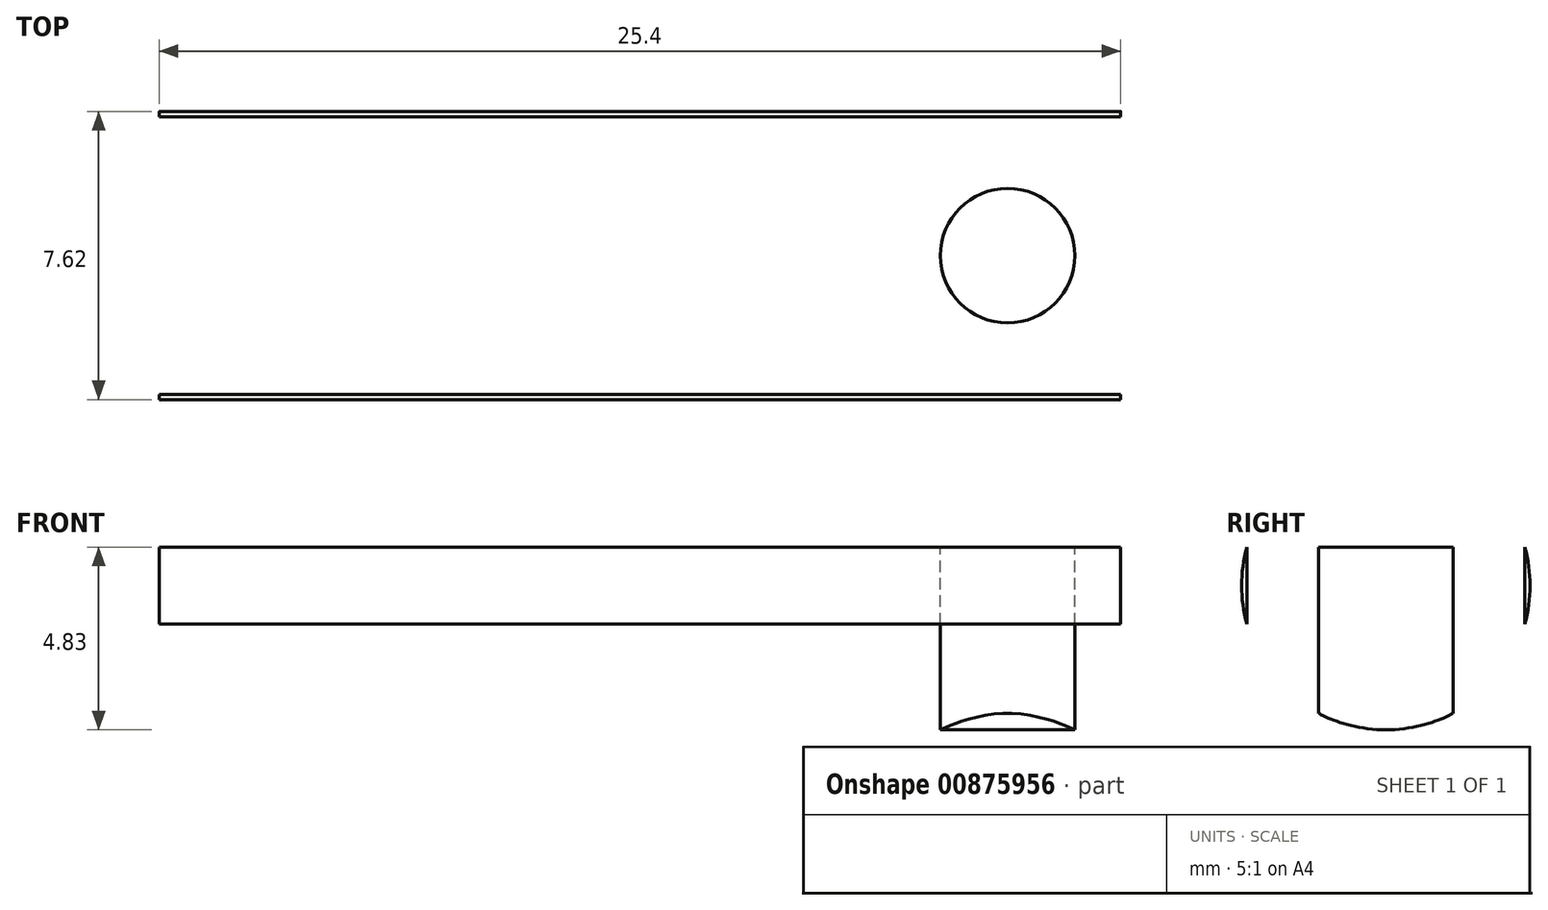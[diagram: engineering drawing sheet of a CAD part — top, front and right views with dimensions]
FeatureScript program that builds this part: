
annotation { "Feature Type Name" : "Feature", "Feature Type Description" : "" }
export const myFeature = defineFeature(function(context is Context, id is Id, definition is map)
    precondition{}
    {
        {
            var Q0;
            Q0=qCreatedBy(makeId("Right.planeOp"),FACE);
            var sketch = newSketch(context, id + "F0", { "sketchPlane" : qUnion([Q0])});
            skCircle(sketch, "E0", {"center": v(0, 0) * mm, "radius": 3.81 * mm});
            skSolve(sketch);
        }
        {
            var Q0;
            Q0=makeQuery(id+"F0.imprint","IMPRINT",FACE,{"disambiguationData":[TD([[makeQuery(id+"F0.imprint","IMPRINT",EDGE,{"derivedFrom":sQuery(id+"F0.wireOp",EDGE,"E0")}),1.0]])]});
            extrude(context, id + "F1", {"entities" : qUnion([Q0]), "endBound" : BoundingType.SYMMETRIC, "depth" : 25.4 * mm, "offsetDistance" : 25.4 * mm});
        }
        {
            var Q0;
            Q0=makeQuery(id+"F1.opExtrude","CAP_FACE",FACE,{"disambiguationData":[OSD([sQuery(id+"F0.wireOp",EDGE,"E0")])],"isStart":false});
            var sketch = newSketch(context, id + "F2", { "sketchPlane" : qUnion([Q0])});
            skLineSegment(sketch, "E1", {"start": v(-3.81, 0) * mm, "end": v(3.81, 0) * mm});
            skLineSegment(sketch, "E2.0", {"start": v(-3.67, 1.02) * mm, "end": v(3.67, 1.02) * mm});
            skArc(sketch, "E3", {"start": v(3.67, 1.02) * mm, "mid": v(0, 3.81) * mm, "end": v(-3.67, 1.02) * mm});
            skPoint(sketch, "E4.orphan", {"position": v(-7.67, 0) * mm});
            skSolve(sketch);
        }
        {
            var Q0;
            Q0=makeQuery(id+"F2.imprint","IMPRINT",FACE,{"disambiguationData":[TD([[makeQuery(id+"F2.imprint","IMPRINT",EDGE,{"derivedFrom":sQuery(id+"F2.wireOp",EDGE,"E2.0")}),1.0]])]});
            extrude(context, id + "F3", {"entities" : qUnion([Q0]), "operationType" : NewBodyOperationType.REMOVE, "oppositeDirection" : true, "depth" : 25.4 * mm, "offsetDistance" : 25.4 * mm});
        }
        {
            var Q0;
            Q0=makeQuery(id+"F3.boolean.opBoolean","COPY",FACE,{"derivedFrom":makeQuery(id+"F3.opExtrude","SWEPT_FACE",FACE,{"disambiguationData":[OSD([sQuery(id+"F2.wireOp",EDGE,"E2.0")])]})});
            var sketch = newSketch(context, id + "F4", { "sketchPlane" : qUnion([Q0])});
            skCircle(sketch, "E5", {"center": v(-9.72, 0) * mm, "radius": 1.78 * mm});
            skCircle(sketch, "E6.MirrorC", {"center": v(9.72, 0) * mm, "radius": 1.78 * mm});
            skSolve(sketch);
        }
        {
            var Q0;
            Q0=makeQuery(id+"F4.imprint","IMPRINT",FACE,{"disambiguationData":[TD([[makeQuery(id+"F4.imprint","IMPRINT",EDGE,{"derivedFrom":sQuery(id+"F4.wireOp",EDGE,"E5")}),1.0]])]});
            var Q1;
            Q1=makeQuery(id+"F4.imprint","IMPRINT",FACE,{"disambiguationData":[TD([[makeQuery(id+"F4.imprint","IMPRINT",EDGE,{"derivedFrom":sQuery(id+"F4.wireOp",EDGE,"E6.MirrorC")}),-1.0]])]});
            extrude(context, id + "F5", {"entities" : qUnion([Q0, Q1]), "operationType" : NewBodyOperationType.REMOVE, "oppositeDirection" : true, "depth" : 25.4 * mm, "offsetDistance" : 25.4 * mm});
        }
        {
            var Q0;
            Q0=makeQuery(id+"F3.boolean.opBoolean","COPY",FACE,{"derivedFrom":makeQuery(id+"F3.opExtrude","SWEPT_FACE",FACE,{"disambiguationData":[OSD([sQuery(id+"F2.wireOp",EDGE,"E2.0")])]})});
            var sketch = newSketch(context, id + "F6", { "sketchPlane" : qUnion([Q0])});
            skLineSegment(sketch, "E7.bottom", {"start": v(4.44, 0.64) * mm, "end": v(-4.45, 0.64) * mm});
            skLineSegment(sketch, "E7.top", {"start": v(4.44, -0.64) * mm, "end": v(-4.45, -0.64) * mm});
            skLineSegment(sketch, "E7.left", {"start": v(4.76, 0.32) * mm, "end": v(4.76, -0.32) * mm});
            skLineSegment(sketch, "E7.right", {"start": v(-4.76, 0.32) * mm, "end": v(-4.76, -0.32) * mm});
            skPoint(sketch, "E7.middle", {"position": v(0, 0) * mm});
            skLineSegment(sketch, "E8.bottom", {"start": v(4.4, -1.65) * mm, "end": v(-4.5, -1.65) * mm});
            skLineSegment(sketch, "E8.top", {"start": v(4.4, -2.92) * mm, "end": v(-4.5, -2.92) * mm});
            skLineSegment(sketch, "E8.left", {"start": v(4.7, -1.97) * mm, "end": v(4.7, -2.6) * mm});
            skLineSegment(sketch, "E8.right", {"start": v(-4.82, -1.97) * mm, "end": v(-4.82, -2.6) * mm});
            skPoint(sketch, "E8.middle", {"position": v(-0.05, -2.29) * mm});
            skLineSegment(sketch, "E9.MirrorCS", {"start": v(4.4, 1.65) * mm, "end": v(-4.5, 1.65) * mm});
            skLineSegment(sketch, "E10.MirrorCS", {"start": v(4.7, 1.97) * mm, "end": v(4.7, 2.6) * mm});
            skLineSegment(sketch, "E11.MirrorCS", {"start": v(4.4, 2.92) * mm, "end": v(-4.5, 2.92) * mm});
            skLineSegment(sketch, "E12.MirrorCS", {"start": v(-4.82, 1.97) * mm, "end": v(-4.82, 2.6) * mm});
            skPoint(sketch, "E13.visualSharp", {"position": v(-4.82, 2.92) * mm});
            skArc(sketch, "E13.filletArc", {"start": v(-4.5, 2.92) * mm, "mid": v(-4.72, 2.83) * mm, "end": v(-4.82, 2.6) * mm});
            skPoint(sketch, "E14.visualSharp", {"position": v(-4.82, 1.65) * mm});
            skArc(sketch, "E14.filletArc", {"start": v(-4.82, 1.97) * mm, "mid": v(-4.72, 1.74) * mm, "end": v(-4.5, 1.65) * mm});
            skPoint(sketch, "E15.visualSharp", {"position": v(4.7, 2.92) * mm});
            skArc(sketch, "E15.filletArc", {"start": v(4.7, 2.6) * mm, "mid": v(4.61, 2.83) * mm, "end": v(4.4, 2.92) * mm});
            skPoint(sketch, "E16.visualSharp", {"position": v(4.7, 1.65) * mm});
            skArc(sketch, "E16.filletArc", {"start": v(4.4, 1.65) * mm, "mid": v(4.61, 1.74) * mm, "end": v(4.7, 1.97) * mm});
            skPoint(sketch, "E17.visualSharp", {"position": v(4.76, 0.64) * mm});
            skArc(sketch, "E17.filletArc", {"start": v(4.76, 0.32) * mm, "mid": v(4.67, 0.54) * mm, "end": v(4.44, 0.64) * mm});
            skPoint(sketch, "E18.visualSharp", {"position": v(4.76, -0.64) * mm});
            skArc(sketch, "E18.filletArc", {"start": v(4.44, -0.64) * mm, "mid": v(4.67, -0.54) * mm, "end": v(4.76, -0.32) * mm});
            skPoint(sketch, "E19.visualSharp", {"position": v(-4.76, -0.64) * mm});
            skArc(sketch, "E19.filletArc", {"start": v(-4.76, -0.32) * mm, "mid": v(-4.67, -0.54) * mm, "end": v(-4.45, -0.64) * mm});
            skPoint(sketch, "E20.visualSharp", {"position": v(-4.76, 0.64) * mm});
            skArc(sketch, "E20.filletArc", {"start": v(-4.45, 0.64) * mm, "mid": v(-4.67, 0.54) * mm, "end": v(-4.76, 0.32) * mm});
            skPoint(sketch, "E21.visualSharp", {"position": v(-4.82, -1.65) * mm});
            skArc(sketch, "E21.filletArc", {"start": v(-4.5, -1.65) * mm, "mid": v(-4.72, -1.74) * mm, "end": v(-4.82, -1.97) * mm});
            skPoint(sketch, "E22.visualSharp", {"position": v(-4.82, -2.92) * mm});
            skArc(sketch, "E22.filletArc", {"start": v(-4.82, -2.6) * mm, "mid": v(-4.72, -2.83) * mm, "end": v(-4.5, -2.92) * mm});
            skPoint(sketch, "E23.visualSharp", {"position": v(4.7, -2.92) * mm});
            skArc(sketch, "E23.filletArc", {"start": v(4.4, -2.92) * mm, "mid": v(4.61, -2.83) * mm, "end": v(4.7, -2.6) * mm});
            skPoint(sketch, "E24.visualSharp", {"position": v(4.7, -1.65) * mm});
            skArc(sketch, "E24.filletArc", {"start": v(4.7, -1.97) * mm, "mid": v(4.61, -1.74) * mm, "end": v(4.4, -1.65) * mm});
            skSolve(sketch);
        }
        {
            var Q0;
            Q0=makeQuery(id+"F6.imprint","IMPRINT",FACE,{"disambiguationData":[TD([[makeQuery(id+"F6.imprint","IMPRINT",EDGE,{"derivedFrom":sQuery(id+"F6.wireOp",EDGE,"E9.MirrorCS")}),-1.0]])]});
            var Q1;
            Q1=makeQuery(id+"F6.imprint","IMPRINT",FACE,{"disambiguationData":[TD([[makeQuery(id+"F6.imprint","IMPRINT",EDGE,{"derivedFrom":sQuery(id+"F6.wireOp",EDGE,"E7.bottom")}),1.0]])]});
            var Q2;
            Q2=makeQuery(id+"F6.imprint","IMPRINT",FACE,{"disambiguationData":[TD([[makeQuery(id+"F6.imprint","IMPRINT",EDGE,{"derivedFrom":sQuery(id+"F6.wireOp",EDGE,"E8.bottom")}),1.0]])]});
            extrude(context, id + "F7", {"entities" : qUnion([Q0, Q1, Q2]), "operationType" : NewBodyOperationType.REMOVE, "oppositeDirection" : true, "depth" : 0.32 * mm, "offsetDistance" : 25.4 * mm});
        }
    });
